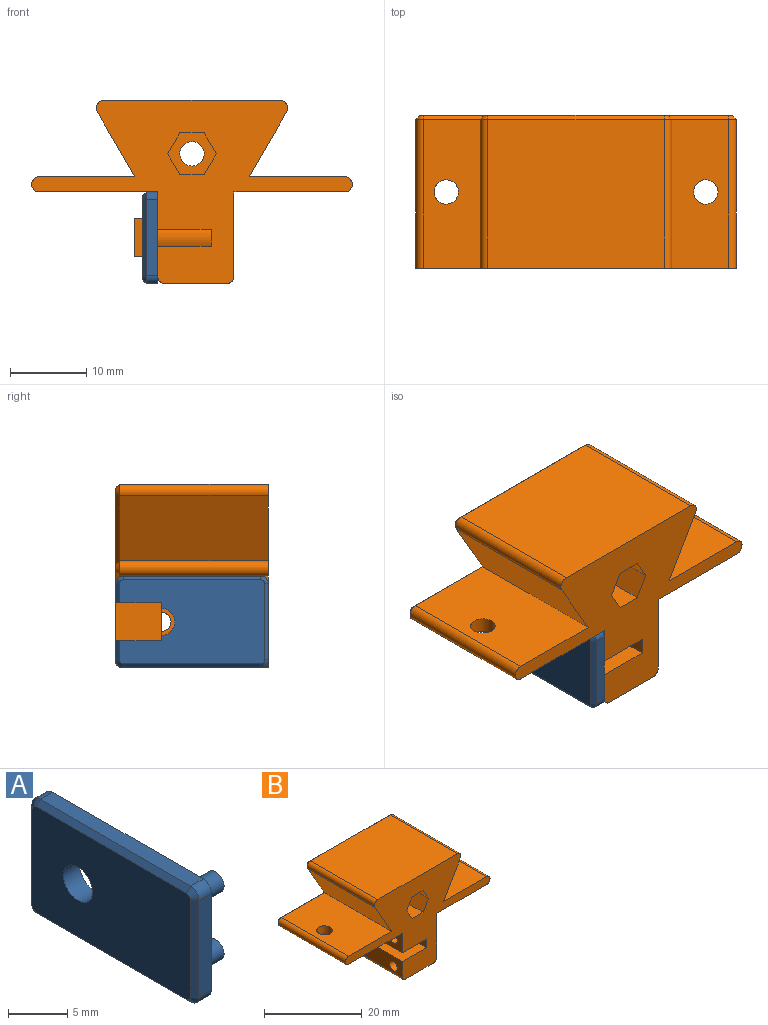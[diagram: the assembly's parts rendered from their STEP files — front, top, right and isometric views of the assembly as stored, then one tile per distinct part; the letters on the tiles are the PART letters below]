
ASSEMBLY  parts=2 mates=1
PART A: 23 faces, bbox 5x20x12 mm
  f0: plane 10x1.5mm, normal (0,-1,0), area 15mm2, adj f5,f11,f14,f18
  f1: plane 18x1.5mm, normal (0,0,-1), area 27mm2, adj f5,f11,f12,f22
  f2: plane 10x1.5mm, normal (0,1,0), area 15mm2, adj f5,f12,f13,f19
  f3: cylinder r=1.75mm len=3.5mm, axis (-1,0,0), area 22mm2, adj f5,f6
  f4: plane 18x1.5mm, normal (0,0,1), area 27mm2, adj f5,f13,f14,f15
  f5: plane 20x12mm, normal (1,0,0), area 223.2mm2, adj f0,f1,f2,f3,f4,f7,f9,f11
  f6: plane 19x11mm, normal (-1,0,0), area 199.2mm2, adj f3,f15,f16,f17,f18,f19,f20,f21
  f7: cylinder r=1mm len=3mm, axis (-1,0,0), area 18.8mm2, adj f5,f8
  f8: plane 2x2mm, normal (1,0,0), area 3.1mm2, adj f7
  f9: cylinder r=1mm len=3mm, axis (-1,0,0), area 18.8mm2, adj f5,f10
  f10: plane 2x2mm, normal (1,0,0), area 3.1mm2, adj f9
  f11: cylinder r=1mm len=1.5mm, axis (-1,0,0), area 2.4mm2, adj f0,f1,f5,f20
  f12: cylinder r=1mm len=1.5mm, axis (1,0,0), area 2.4mm2, adj f1,f2,f5,f21
  f13: cylinder r=1mm len=1.5mm, axis (-1,0,0), area 2.4mm2, adj f2,f4,f5,f17
  f14: cylinder r=1mm len=1.5mm, axis (1,0,0), area 2.4mm2, adj f0,f4,f5,f16
  f15: plane 18x0.5mm, normal (-0.71,0,0.71), area 12.7mm2, adj f4,f6,f16,f17
  f16: cone r=0.5mm half-angle=45deg, axis (1,0,0), area 0.8mm2, adj f6,f14,f15,f18
  f17: cone r=0.5mm half-angle=45deg, axis (1,0,0), area 0.8mm2, adj f6,f13,f15,f19
  f18: plane 10x0.5mm, normal (-0.71,-0.71,0), area 7.1mm2, adj f0,f6,f16,f20
  f19: plane 10x0.5mm, normal (-0.71,0.71,0), area 7.1mm2, adj f2,f6,f17,f21
  f20: cone r=0.5mm half-angle=45deg, axis (1,0,0), area 0.8mm2, adj f6,f11,f18,f22
  f21: cone r=0.5mm half-angle=45deg, axis (1,0,0), area 0.8mm2, adj f6,f12,f19,f22
  f22: plane 18x0.5mm, normal (-0.71,0,-0.71), area 12.7mm2, adj f1,f6,f20,f21
PART B: 63 faces, bbox 42x20x24 mm
  f0: plane 42x24mm, normal (0,-1,0), area 367.5mm2, adj f2,f3,f4,f5,f6,f7,f8,f9
  f1: plane 5x4.4mm, normal (-1,0,0), area 10.6mm2, adj f18,f24,f25,f26
  f2: plane 19.5x11mm, normal (-1,0,0), area 133.8mm2, adj f0,f5,f15,f16,f17,f20,f22,f43
  f3: plane 19.5x8.5mm, normal (-0.87,0,-0.5), area 191.4mm2, adj f0,f4,f13,f54
  f4: plane 19.5x12.5mm, normal (0,0,1), area 235.7mm2, adj f0,f3,f34,f46,f52
  f5: plane 19.5x15.5mm, normal (0,0,-1), area 294.2mm2, adj f0,f2,f34,f46,f48
  f6: plane 19.5x8mm, normal (0,0,-1), area 156mm2, adj f0,f43,f44,f51
  f7: plane 19.5x11mm, normal (1,0,0), area 209.6mm2, adj f0,f8,f24,f44,f55
  f8: plane 19.5x14.5mm, normal (0,0,-1), area 274.7mm2, adj f0,f7,f33,f45,f57
  f9: plane 19.5x12.5mm, normal (0,0,1), area 235.7mm2, adj f0,f10,f33,f45,f61
  f10: plane 19.5x8.5mm, normal (0.87,0,-0.5), area 191.4mm2, adj f0,f9,f11,f62
  f11: cylinder r=1mm len=19.5mm, axis (0,1,0), area 40.8mm2, adj f0,f10,f12,f60
  f12: plane 23.08x19.5mm, normal (0,0,1), area 450.1mm2, adj f0,f11,f13,f58
  f13: cylinder r=1mm len=19.5mm, axis (0,1,0), area 40.8mm2, adj f0,f3,f12,f56
  f14: plane 41x23mm, normal (0,1,0), area 330.7mm2, adj f42,f47,f48,f49,f50,f51,f52,f53
  f15: plane 10.15x7mm, normal (0,0,-1), area 71.1mm2, adj f0,f2,f16,f19
  f16: cylinder r=4mm len=8mm, axis (-1,0,0), area 160.3mm2, adj f2,f15,f17,f19
  f17: plane 10.15x7mm, normal (0,0,1), area 71.1mm2, adj f0,f2,f16,f19
  f18: cylinder r=2.5mm len=8mm, axis (-1,0,0), area 117.8mm2, adj f1,f19,f25,f27
  f19: plane 18x8mm, normal (-1,0,0), area 52.7mm2, adj f0,f15,f16,f17,f18
  f20: cylinder r=1.15mm len=7mm, axis (-1,0,0), area 50.6mm2, adj f2,f21
  f21: plane 2.3x2.3mm, normal (-1,0,0), area 4.2mm2, adj f20
  f22: cylinder r=1.15mm len=7mm, axis (-1,0,0), area 50.6mm2, adj f2,f23
  f23: plane 2.3x2.3mm, normal (-1,0,0), area 4.2mm2, adj f22
  f24: cylinder r=1.25mm len=10mm, axis (-1,0,0), area 78.5mm2, adj f1,f7
  f25: plane 5x3mm, normal (0,-1,0), area 11.2mm2, adj f1,f18,f26,f28,f29,f31,f32
  f26: cylinder r=1.9mm len=3.8mm, axis (1,0,0), area 6mm2, adj f1,f25,f32
  f27: plane 6x5mm, normal (1,0,0), area 20.2mm2, adj f18,f28,f29,f30
  f28: plane 6x2mm, normal (0,0,-1), area 12mm2, adj f25,f27,f30,f31
  f29: plane 6x2mm, normal (0,0,1), area 12mm2, adj f25,f27,f30,f31
  f30: plane 5x2mm, normal (0,1,0), area 10mm2, adj f27,f28,f29,f31
  f31: plane 6x5mm, normal (-1,0,0), area 30mm2, adj f25,f28,f29,f30
  f32: plane 3.8x1.9mm, normal (1,0,0), area 5.7mm2, adj f25,f26
  f33: cylinder r=1.6mm len=3.2mm, axis (0,0,1), area 20.1mm2, adj f8,f9
  f34: cylinder r=1.6mm len=3.2mm, axis (0,0,1), area 20.1mm2, adj f4,f5
  f35: plane 5x2.75mm, normal (-0.87,0,0.5), area 15.9mm2, adj f0,f36,f40,f41
  f36: plane 5x2.75mm, normal (-0.87,0,-0.5), area 15.9mm2, adj f0,f35,f37,f41
  f37: plane 5x3.18mm, normal (0,0,-1), area 15.9mm2, adj f0,f36,f38,f41
  f38: plane 5x2.75mm, normal (0.87,0,-0.5), area 15.9mm2, adj f0,f37,f39,f41
  f39: plane 5x2.75mm, normal (0.87,0,0.5), area 15.9mm2, adj f0,f38,f40,f41
  f40: plane 5x3.18mm, normal (0,0,1), area 15.9mm2, adj f0,f35,f39,f41
  f41: plane 6.35x5.5mm, normal (0,-1,0), area 18.2mm2, adj f35,f36,f37,f38,f39,f40,f42
  f42: cylinder r=1.6mm len=15mm, axis (0,-1,0), area 150.8mm2, adj f14,f41
  f43: cylinder r=1mm len=19.5mm, axis (0,1,0), area 30.6mm2, adj f0,f2,f6,f49
  f44: cylinder r=1mm len=19.5mm, axis (0,-1,0), area 30.6mm2, adj f0,f6,f7,f53
  f45: cylinder r=1mm len=19.5mm, axis (0,-1,0), area 61.3mm2, adj f0,f8,f9,f59
  f46: cylinder r=1mm len=19.5mm, axis (0,1,0), area 61.3mm2, adj f0,f4,f5,f50
  f47: plane 11.5x0.5mm, normal (-0.71,0.71,0), area 8mm2, adj f2,f14,f48,f49
  f48: plane 16x0.5mm, normal (0,0.71,-0.71), area 11.1mm2, adj f5,f14,f47,f50
  f49: cone r=0.5mm half-angle=45deg, axis (0,-1,0), area 0.8mm2, adj f14,f43,f47,f51
  f50: cone r=0.5mm half-angle=45deg, axis (0,-1,0), area 1.7mm2, adj f14,f46,f48,f52
  f51: plane 8x0.5mm, normal (0,0.71,-0.71), area 5.7mm2, adj f6,f14,f49,f53
  f52: plane 13.37x0.5mm, normal (0,0.71,0.71), area 9.1mm2, adj f4,f14,f50,f54
  f53: cone r=0.5mm half-angle=45deg, axis (0,-1,0), area 0.8mm2, adj f14,f44,f51,f55
  f54: plane 9.25x5.77mm, normal (-0.61,0.71,-0.35), area 7.2mm2, adj f3,f14,f52,f56
  f55: plane 11.5x0.5mm, normal (0.71,0.71,0), area 8mm2, adj f7,f14,f53,f57
  f56: cone r=1mm half-angle=45deg, axis (0,-1,0), area 1.1mm2, adj f13,f14,f54,f58
  f57: plane 15x0.5mm, normal (0,0.71,-0.71), area 10.4mm2, adj f8,f14,f55,f59
  f58: plane 23.08x0.5mm, normal (0,0.71,0.71), area 16.3mm2, adj f12,f14,f56,f60
  f59: cone r=0.5mm half-angle=45deg, axis (0,-1,0), area 1.7mm2, adj f14,f45,f57,f61
  f60: cone r=1mm half-angle=45deg, axis (0,-1,0), area 1.1mm2, adj f11,f14,f58,f62
  f61: plane 13.37x0.5mm, normal (0,0.71,0.71), area 9.1mm2, adj f9,f14,f59,f62
  f62: plane 9.25x5.77mm, normal (0.61,0.71,-0.35), area 7.2mm2, adj f10,f14,f60,f61
PLACE A t=(-21.28,-16.9,-10.53)mm
PLACE B t=(-39.78,-16.9,-10.53)mm
MATE fastened B.f16 <-> A.f3  axis (-1,0,0) through (-44.28,-22.9,-17.53)mm
